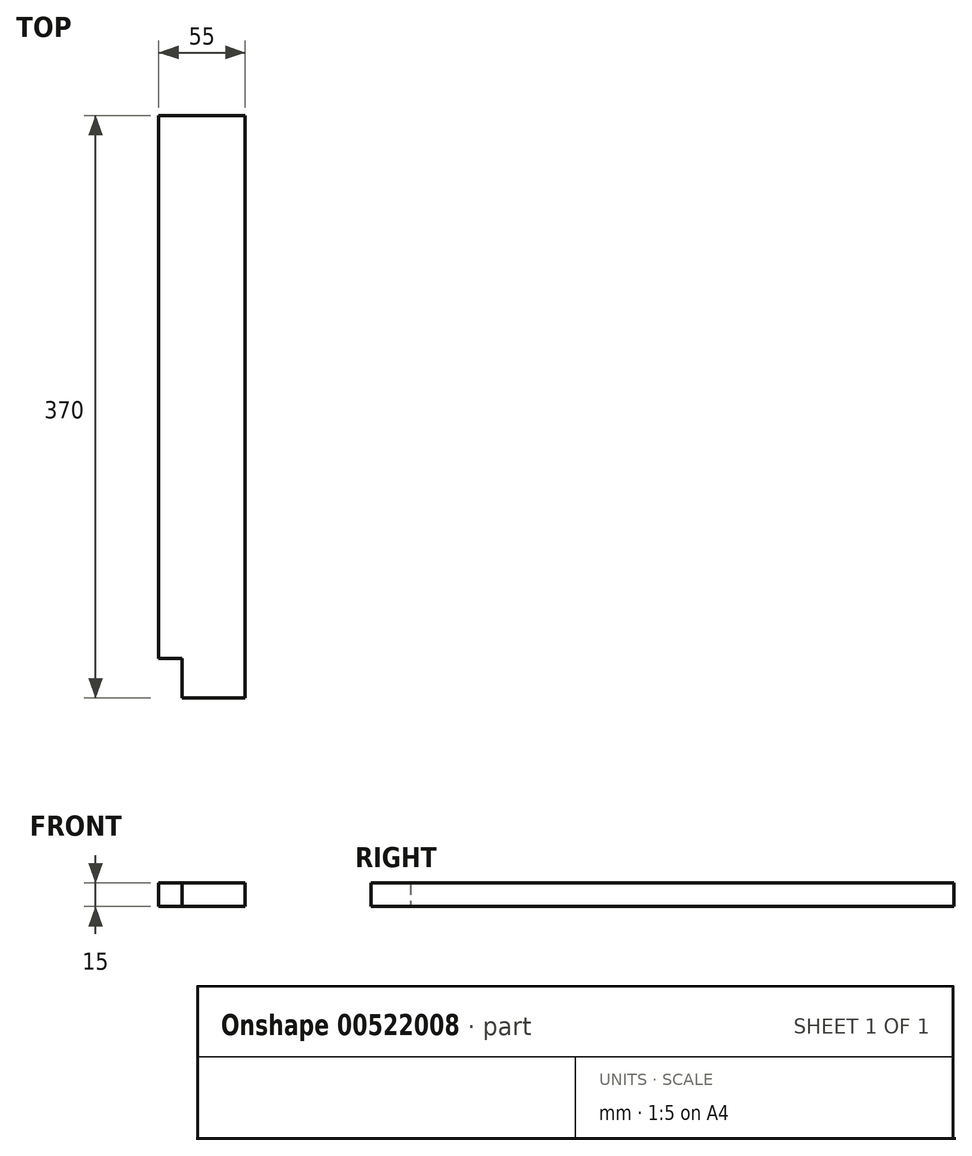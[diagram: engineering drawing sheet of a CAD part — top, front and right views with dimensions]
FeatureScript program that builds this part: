
annotation { "Feature Type Name" : "Feature", "Feature Type Description" : "" }
export const myFeature = defineFeature(function(context is Context, id is Id, definition is map)
    precondition{}
    {
        {
            var Q0;
            Q0=qCreatedBy(makeId("Top.planeOp"),FACE);
            var sketch = newSketch(context, id + "F0", { "sketchPlane" : qUnion([Q0])});
            skLineSegment(sketch, "E0.bottom", {"start": v(0, 0) * mm, "end": v(40, 0) * mm});
            skLineSegment(sketch, "E0.top", {"start": v(-15, 370) * mm, "end": v(40, 370) * mm});
            skLineSegment(sketch, "E0.left", {"start": v(-15, 25) * mm, "end": v(-15, 370) * mm});
            skLineSegment(sketch, "E0.right", {"start": v(40, 0) * mm, "end": v(40, 370) * mm});
            skLineSegment(sketch, "E1", {"start": v(-15, 25) * mm, "end": v(0, 25) * mm});
            skLineSegment(sketch, "E2", {"start": v(0, 25) * mm, "end": v(0, 0) * mm});
            skSolve(sketch);
        }
        {
            var Q0;
            Q0=makeQuery(id+"F0.imprint","IMPRINT",FACE,{"disambiguationData":[TD([[makeQuery(id+"F0.imprint","IMPRINT",EDGE,{"derivedFrom":sQuery(id+"F0.wireOp",EDGE,"E0.bottom")}),1.0]])]});
            extrude(context, id + "F1", {"entities" : qUnion([Q0]), "depth" : 15 * mm, "offsetDistance" : 25 * mm});
        }
    });
